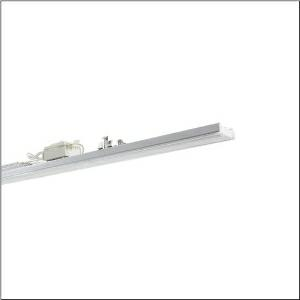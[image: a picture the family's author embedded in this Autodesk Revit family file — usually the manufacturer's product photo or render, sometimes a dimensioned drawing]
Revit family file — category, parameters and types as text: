
# Revit family: licross_r__11_recessed_mo_51tl12dnd9xg_c455
name_source: partatom
category: Lighting Fixtures
units: mm (PartAtom-declared; Revit-internal decimal feet)

## family parameters
Cut with Voids When Loaded = No
Host = Face
Light Source = No
Part Type = Normal
Room Calculation Point = No
Round Connector Dimension = Use Diameter
Shared = No

## types (1)
- --- (1 x LED, 9310 lm, 56.2 W, 4000K)
    Apparent Load = 56 VA
    CIE Flux Codes = 67 92 99 100 100
    Color Rendering = 90
    Color Temperature = 4000K
    Default Elevation = 1800 mm
    Description = Licross® 11 Recessed MO, luminaire insert, of sheet steel, coil coated, white, length: 1.500mm, width: 66mm, height: 67mm, LED rated luminous flux: 9.310lm, light colour: 940, control gear: DALI 2, with plug, 5-pole, with phase selection, mains connection: 220..240V, AC, 50/60Hz, rated input power: 56W, halogen-free wiring, primary optical cover: cover, of PMMA, light emission: direct distribution, primary light characteristic: symmetric, protection rating (complete): IP40, insulation class (complete): insulation class I (protective earthing), certification: CE, ENEC, VDE, UKCA, protection symbol: D if used in an environment without relevant dust loads with corresponding accessories, impact resistance: IK06, permissible ambient temperature for indoor applications: -25..+45°C, corresponds to IFS (International Featured Standards) requirements for safety and quality in the food industry, reducing of maximum allowable ambient temperature of 5°C with ceiling mounting, LABS conformity tested according to VDMA 24364:2018-05, packaging unit: 1 piece
    Height = 58 mm
    Lamp = 1 x LED
    Lamp Light Flux = 9310 lm
    Lamp Power = 56.2 W
    Lamp count = 1
    Length = 1500 mm
    Luminous efficacy = 166 lm/W
    Manufacturer = Siteco
    ModVariant = No
    Model = 51TL12DND9XG
    Mounting Place = Ceiling
    Mounting Type = Pendant
    Number of Poles = 1
    OnlyDefault = Yes
    Power Factor = 1
    Product Name = Licross® 11 Recessed MO
    Product group = luminaire insert
    ProductGroupID = 902
    Protection Class = Protection class I
    Protection Degree = IP 40
    RLX_Detail_Level = 1
    RLX_Emergency_Light_Flux = 0 lm
    RLX_Emergency_Type = 0
    RLX_Emergency_Type_DB = No
    RlxData = <blob elided: 24469 chars, md5=59dfafb3>
    Socket = socket
    Standby Power = 0 W
    System Light Flux = 9310 lm
    System Power = 56 W
    Type Comments = factory setting: luminous flux: 100 % | dim-lin: 254 | 378 mA
    Type Image = l_1296930.jpg
    URL = http://relux.com
    VarID = @adj_049046
    Voltage = 0 V
    Weight = 0.00 kg
    Width = 66 mm

## geometry (parser evidence)
native form markers: Blend x4, Sweep x11
no freeform markers — native parametric forms only
